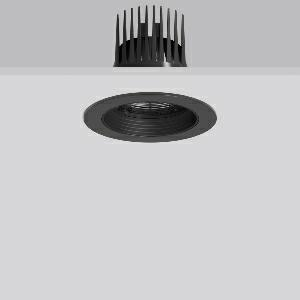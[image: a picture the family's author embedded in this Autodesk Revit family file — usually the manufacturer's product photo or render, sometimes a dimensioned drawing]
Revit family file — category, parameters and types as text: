
# Revit family: heledon_maxi_e_901760_003_76_afd5
name_source: partatom
category: Lighting Fixtures
units: mm (PartAtom-declared; Revit-internal decimal feet)

## family parameters
Cut with Voids When Loaded = No
Host = Face
Light Source = No
Part Type = Normal
Room Calculation Point = No
Round Connector Dimension = Use Diameter
Shared = No

## types (1)
- HELEDON maxi E (1 x LED Modul 930, 2850 lm, 3000)
    Apparent Load = 25 VA
    Approval mark = CE
    CIE Flux Codes = 97 100 100 100 100
    Color Rendering = 90
    Color Temperature = 3000
    Default Elevation = 1800 mm
    Description = Series: HELEDON maxi
Round recessed downlight. Housing: die-cast aluminium, powder-coated. Black plastic ring and recessed LED to prevent glare from the side. Optical assembly with lens made of plastic (polycarbonate) for the best homogeneous light distribution - can be changed without tools. Best colour rendering index Ra>90. Suitable for Recessed ceiling mounting. Installation without tools thanks to spring fastening system. Including separate LED converter with connecting cable 600 mm.High quality converter without flickering and stroboscopic effect. Through-wiring box (5 pole) available as accessory. The following accessories can be mounted without use of tools: interchangeable lenses, decorative glasses, honeycomb louvre, clear and frosted diffusers, white interchangeable plastic ring. 
Colour: deep black, matt (RAL 9005)
Diameter: 162 mm
Height: 3 mm
Cut-out diameter: 152 mm
Recess height: 200 mm
Luminaire: recess height: 135 mm
Lamp: LED
Socket: without socket
Colour temperature: 3000K
Colour rendering index (CRI): 92
System power: 25 W
Rated luminous flux: 2850 lm
Luminous efficiency: 114 lm/W
Control gear: Converter, dimmable, DALI
Protection class: II
Type of protection: IP 20
    Height = 0 mm  [stored 0 ft]
    Lamp = 1 x LED Modul 930
    Lamp Light Flux = 2850 lm
    Lamp count = 1
    Length = 162 mm
    Lifetime = 50000 h
    Luminous efficacy = 114 lm/W
    Manufacturer = RZB
    ModVariant = No
    Model = 901760.003.76
    Mounting Place = Ceiling
    Mounting Type = Recessed
    Number of Poles = 1
    OnlyDefault = Yes
    Power Factor = 1
    Product Name = HELEDON maxi E
    Product group = Recessed downlights
    ProductGroupID = 402
    Protection Class = Protection class II
    Protection Degree = IP 20
    RLX_Detail_Level = 1
    RLX_Emergency_Light_Flux = 0 lm
    RLX_Emergency_Type = 0
    RLX_Emergency_Type_DB = No
    RlxData = <blob elided: 122169 chars, md5=534a3fe9>
    Socket = socket
    Standby Power = 0 W
    System Light Flux = 2850 lm
    System Power = 25 W
    Type Comments = Product without accessories
    Type Image = 901663.003.jpg
    URL = http://relux.com
    VarID = ---
    Voltage = 230 V
    Voltage Range = 220-240 V
    Weight = 0.00 kg
    Width = 0 mm  [stored 0 ft]

note: [stored X ft] marks values corroborated as IEEE doubles in the binary element streams (Revit-internal decimal feet)

## geometry (parser evidence)
native form markers: Blend x4, Sweep x11
no freeform markers — native parametric forms only
